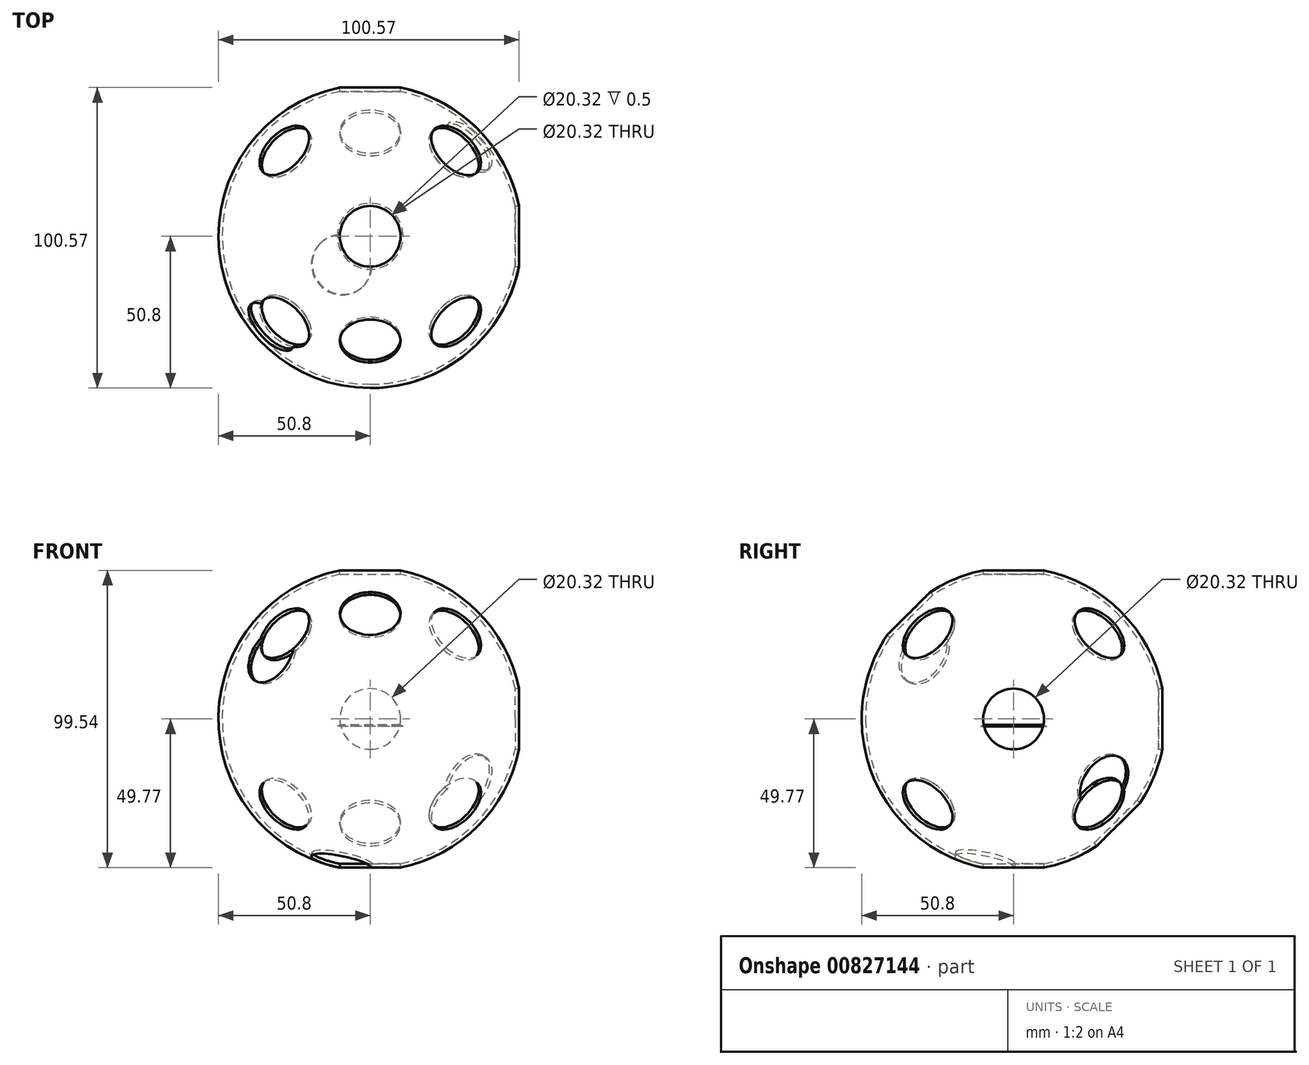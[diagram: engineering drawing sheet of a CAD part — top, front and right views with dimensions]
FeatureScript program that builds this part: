
annotation { "Feature Type Name" : "Feature", "Feature Type Description" : "" }
export const myFeature = defineFeature(function(context is Context, id is Id, definition is map)
    precondition{}
    {
        {
            assignVariable(context, id + "F0", {"name" : "SphereDiameter", "anyValue" : 4});
        }
        {
            assignVariable(context, id + "F1", {"name" : "BaseHeight", "anyValue" : getVariable(context, 'SphereDiameter') / 8});
        }
        {
            var Q0;
            Q0=qCreatedBy(makeId("Top.planeOp"),FACE);
            var sketch = newSketch(context, id + "F2", { "sketchPlane" : qUnion([Q0])});
            skArc(sketch, "E0", {"start": v(0, 50.8) * mm, "mid": v(-50.8, 0) * mm, "end": v(0, -50.8) * mm});
            skLineSegment(sketch, "E1", {"start": v(0, 50.8) * mm, "end": v(0, -50.8) * mm});
            skSolve(sketch);
        }
        {
            var Q0;
            Q0=qSketchRegion(id+"F2",true);
            var Q1;
            Q1=sQuery(id+"F2.wireOp",EDGE,"E1");
            revolve(context, id + "F3", {"surfaceOperationType" : NewSurfaceOperationType.NEW, "entities" : qUnion([Q0]), "axis" : qUnion([Q1]), "revolveType" : RevolveType.FULL});
        }
        {
            var Q0;
            Q0=qCreatedBy(makeId("Top.planeOp"),FACE);
            var sketch = newSketch(context, id + "F4", { "sketchPlane" : qUnion([Q0])});
            skLineSegment(sketch, "E2", {"start": v(0, 0) * mm, "end": v(0, 50.8) * mm});
            skLineSegment(sketch, "E3", {"start": v(0, 0) * mm, "end": v(0, -50.8) * mm});
            skLineSegment(sketch, "E4", {"start": v(0, 0) * mm, "end": v(50.8, 0) * mm});
            skLineSegment(sketch, "E5", {"start": v(0, 0) * mm, "end": v(-50.8, 0) * mm});
            skSolve(sketch);
        }
        {
            var Q0;
            Q0=qCreatedBy(makeId("Front.planeOp"),FACE);
            var sketch = newSketch(context, id + "F5", { "sketchPlane" : qUnion([Q0])});
            skLineSegment(sketch, "E6", {"start": v(0, 0) * mm, "end": v(0, 50.8) * mm});
            skLineSegment(sketch, "E7", {"start": v(0, 0) * mm, "end": v(0, -50.8) * mm});
            skSolve(sketch);
        }
        {
            var Q0;
            Q0=sQuery(id+"F5.wireOp",VERTEX,"E6.end");
            var Q1;
            Q1=sQuery(id+"F4.wireOp",VERTEX,"E3.end");
            var Q2;
            Q2=sQuery(id+"F4.wireOp",VERTEX,"E4.end");
            cPlane(context, id + "F6", {"entities" : qUnion([Q0, Q1, Q2]), "cplaneType" : CPlaneType.THREE_POINT, "offset" : 25.4 * mm, "width" : 152.4 * mm, "height" : 152.4 * mm});
        }
        {
            var Q0;
            Q0=qCreatedBy(id+"F6.planeOp",FACE);
            var sketch = newSketch(context, id + "F7", { "sketchPlane" : qUnion([Q0])});
            skLineSegment(sketch, "E8", {"start": v(-41.48, 0) * mm, "end": v(20.74, -35.92) * mm});
            skLineSegment(sketch, "E9", {"start": v(20.74, -35.92) * mm, "end": v(20.74, 35.92) * mm});
            skLineSegment(sketch, "E10", {"start": v(20.74, 35.92) * mm, "end": v(-41.48, 0) * mm});
            skLineSegment(sketch, "E11", {"start": v(20.74, 35.92) * mm, "end": v(0, 0) * mm});
            skSolve(sketch);
        }
        {
            var Q0;
            Q0=sQuery(id+"F5.wireOp",VERTEX,"E6.end");
            var Q1;
            Q1=sQuery(id+"F7.wireOp",VERTEX,"E11.end");
            var Q2;
            Q2=sQuery(id+"F4.wireOp",VERTEX,"E3.start");
            cPlane(context, id + "F8", {"entities" : qUnion([Q0, Q1, Q2]), "cplaneType" : CPlaneType.THREE_POINT, "offset" : 25.4 * mm, "width" : 152.4 * mm, "height" : 152.4 * mm});
        }
        {
            var Q0;
            Q0=qCreatedBy(id+"F8.planeOp",FACE);
            var sketch = newSketch(context, id + "F9", { "sketchPlane" : qUnion([Q0])});
            skLineSegment(sketch, "E12", {"start": v(0, 0) * mm, "end": v(23.95, 16.93) * mm});
            skLineSegment(sketch, "E13", {"start": v(10.37, 7.33) * mm, "end": v(23.95, 16.93) * mm});
            skLineSegment(sketch, "E14", {"start": v(0, 0) * mm, "end": v(-10.37, -7.33) * mm});
            skSolve(sketch);
        }
        {
            var Q0;
            Q0=sQuery(id+"F4.wireOp",VERTEX,"E2.end");
            var Q1;
            Q1=sQuery(id+"F5.wireOp",VERTEX,"E6.end");
            var Q2;
            Q2=sQuery(id+"F4.wireOp",VERTEX,"E5.end");
            cPlane(context, id + "F10", {"entities" : qUnion([Q0, Q1, Q2]), "cplaneType" : CPlaneType.THREE_POINT, "offset" : 25.4 * mm, "width" : 152.4 * mm, "height" : 152.4 * mm});
        }
        {
            var Q0;
            Q0=qCreatedBy(id+"F10.planeOp",FACE);
            var sketch = newSketch(context, id + "F11", { "sketchPlane" : qUnion([Q0])});
            skLineSegment(sketch, "E15", {"start": v(41.48, 0) * mm, "end": v(-20.74, 35.92) * mm});
            skLineSegment(sketch, "E16", {"start": v(-20.74, 35.92) * mm, "end": v(-20.74, -35.92) * mm});
            skLineSegment(sketch, "E17", {"start": v(-20.74, -35.92) * mm, "end": v(41.48, 0) * mm});
            skLineSegment(sketch, "E18", {"start": v(-20.74, 35.92) * mm, "end": v(0, 0) * mm});
            skSolve(sketch);
        }
        {
            var Q0;
            Q0=sQuery(id+"F5.wireOp",VERTEX,"E6.end");
            var Q1;
            Q1=qCreatedBy(makeId("Origin.pointOp"),VERTEX);
            var Q2;
            Q2=sQuery(id+"F11.wireOp",VERTEX,"E18.end");
            cPlane(context, id + "F12", {"entities" : qUnion([Q0, Q1, Q2]), "cplaneType" : CPlaneType.THREE_POINT, "offset" : 25.4 * mm, "width" : 152.4 * mm, "height" : 152.4 * mm});
        }
        {
            var Q0;
            Q0=qCreatedBy(id+"F12.planeOp",FACE);
            var sketch = newSketch(context, id + "F13", { "sketchPlane" : qUnion([Q0])});
            skLineSegment(sketch, "E19", {"start": v(0, 0) * mm, "end": v(-23.95, 16.93) * mm});
            skLineSegment(sketch, "E20", {"start": v(-23.95, 16.93) * mm, "end": v(-10.37, 7.33) * mm});
            skLineSegment(sketch, "E21", {"start": v(10.37, -7.33) * mm, "end": v(0, 0) * mm});
            skSolve(sketch);
        }
        {
            var Q0;
            Q0=sQuery(id+"F4.wireOp",VERTEX,"E2.end");
            var Q1;
            Q1=sQuery(id+"F5.wireOp",VERTEX,"E7.end");
            var Q2;
            Q2=sQuery(id+"F4.wireOp",VERTEX,"E4.end");
            cPlane(context, id + "F14", {"entities" : qUnion([Q0, Q1, Q2]), "cplaneType" : CPlaneType.THREE_POINT, "offset" : 25.4 * mm, "width" : 152.4 * mm, "height" : 152.4 * mm});
        }
        {
            var Q0;
            Q0=qCreatedBy(id+"F14.planeOp",FACE);
            var sketch = newSketch(context, id + "F15", { "sketchPlane" : qUnion([Q0])});
            skLineSegment(sketch, "E22", {"start": v(20.74, -35.92) * mm, "end": v(20.74, 35.92) * mm});
            skLineSegment(sketch, "E23", {"start": v(20.74, 35.92) * mm, "end": v(-41.48, 0) * mm});
            skLineSegment(sketch, "E24", {"start": v(-41.48, 0) * mm, "end": v(20.74, -35.92) * mm});
            skLineSegment(sketch, "E25", {"start": v(20.74, 35.92) * mm, "end": v(0, 0) * mm});
            skSolve(sketch);
        }
        {
            var Q0;
            Q0=sQuery(id+"F4.wireOp",VERTEX,"E3.start");
            var Q1;
            Q1=sQuery(id+"F4.wireOp",VERTEX,"E2.end");
            var Q2;
            Q2=sQuery(id+"F15.wireOp",VERTEX,"E25.end");
            cPlane(context, id + "F16", {"entities" : qUnion([Q0, Q1, Q2]), "cplaneType" : CPlaneType.THREE_POINT, "offset" : 25.4 * mm, "width" : 152.4 * mm, "height" : 152.4 * mm});
        }
        {
            var Q0;
            Q0=qCreatedBy(id+"F16.planeOp",FACE);
            var sketch = newSketch(context, id + "F17", { "sketchPlane" : qUnion([Q0])});
            skLineSegment(sketch, "E26", {"start": v(0, 0) * mm, "end": v(16.93, -23.95) * mm});
            skLineSegment(sketch, "E27", {"start": v(7.33, -10.37) * mm, "end": v(16.93, -23.95) * mm});
            skLineSegment(sketch, "E28", {"start": v(0, 0) * mm, "end": v(-7.33, 10.37) * mm});
            skSolve(sketch);
        }
        {
            var Q0;
            Q0=sQuery(id+"F5.wireOp",VERTEX,"E6.end");
            var Q1;
            Q1=sQuery(id+"F4.wireOp",VERTEX,"E4.end");
            var Q2;
            Q2=sQuery(id+"F4.wireOp",VERTEX,"E2.end");
            cPlane(context, id + "F18", {"entities" : qUnion([Q0, Q1, Q2]), "cplaneType" : CPlaneType.THREE_POINT, "offset" : 25.4 * mm, "width" : 152.4 * mm, "height" : 152.4 * mm});
        }
        {
            var Q0;
            Q0=qCreatedBy(id+"F18.planeOp",FACE);
            var sketch = newSketch(context, id + "F19", { "sketchPlane" : qUnion([Q0])});
            skLineSegment(sketch, "E29", {"start": v(-20.74, 35.92) * mm, "end": v(41.48, 0) * mm});
            skLineSegment(sketch, "E30", {"start": v(41.48, 0) * mm, "end": v(-20.74, -35.92) * mm});
            skLineSegment(sketch, "E31", {"start": v(-20.74, -35.92) * mm, "end": v(-20.74, 35.92) * mm});
            skLineSegment(sketch, "E32", {"start": v(-20.74, 35.92) * mm, "end": v(0, 0) * mm});
            skSolve(sketch);
        }
        {
            var Q0;
            Q0=sQuery(id+"F5.wireOp",VERTEX,"E6.end");
            var Q1;
            Q1=sQuery(id+"F19.wireOp",VERTEX,"E32.end");
            var Q2;
            Q2=sQuery(id+"F4.wireOp",VERTEX,"E3.start");
            cPlane(context, id + "F20", {"entities" : qUnion([Q0, Q1, Q2]), "cplaneType" : CPlaneType.THREE_POINT, "offset" : 25.4 * mm, "width" : 152.4 * mm, "height" : 152.4 * mm});
        }
        {
            var Q0;
            Q0=qCreatedBy(id+"F20.planeOp",FACE);
            var sketch = newSketch(context, id + "F21", { "sketchPlane" : qUnion([Q0])});
            skLineSegment(sketch, "E33", {"start": v(0, 0) * mm, "end": v(23.95, 16.93) * mm});
            skLineSegment(sketch, "E34", {"start": v(10.37, 7.33) * mm, "end": v(23.95, 16.93) * mm});
            skLineSegment(sketch, "E35", {"start": v(0, 0) * mm, "end": v(-10.37, -7.33) * mm});
            skSolve(sketch);
        }
        {
            var Q0;
            Q0=qCreatedBy(makeId("Top.planeOp"),FACE);
            var Q1;
            Q1=sQuery(id+"F5.wireOp",VERTEX,"E6.end");
            cPlane(context, id + "F22", {"entities" : qUnion([Q0, Q1]), "cplaneType" : CPlaneType.PLANE_POINT, "offset" : 25.4 * mm, "width" : 152.4 * mm, "height" : 152.4 * mm});
        }
        {
            var Q0;
            Q0=qCreatedBy(id+"F22.planeOp",FACE);
            var sketch = newSketch(context, id + "F23", { "sketchPlane" : qUnion([Q0])});
            skCircle(sketch, "E36", {"center": v(0, 0) * mm, "radius": 10.16 * mm});
            skSolve(sketch);
        }
        {
            var Q0;
            Q0=qSketchRegion(id+"F23",true);
            extrude(context, id + "F24", {"entities" : qUnion([Q0]), "operationType" : NewBodyOperationType.REMOVE, "endBound" : BoundingType.SYMMETRIC, "oppositeDirection" : true, "depth" : 76.2 * mm, "offsetDistance" : 25.4 * mm});
        }
        {
            var Q0;
            Q0=qCreatedBy(makeId("Right.planeOp"),FACE);
            var Q1;
            Q1=sQuery(id+"F4.wireOp",VERTEX,"E4.end");
            cPlane(context, id + "F25", {"entities" : qUnion([Q0, Q1]), "cplaneType" : CPlaneType.PLANE_POINT, "offset" : 25.4 * mm, "width" : 152.4 * mm, "height" : 152.4 * mm});
        }
        {
            var Q0;
            Q0=qCreatedBy(id+"F25.planeOp",FACE);
            var sketch = newSketch(context, id + "F26", { "sketchPlane" : qUnion([Q0])});
            skCircle(sketch, "E37", {"center": v(0, 0) * mm, "radius": 10.16 * mm});
            skSolve(sketch);
        }
        {
            var Q0;
            Q0=qSketchRegion(id+"F26",true);
            extrude(context, id + "F27", {"entities" : qUnion([Q0]), "operationType" : NewBodyOperationType.REMOVE, "endBound" : BoundingType.SYMMETRIC, "oppositeDirection" : true, "depth" : 76.2 * mm, "offsetDistance" : 25.4 * mm});
        }
        {
            var Q0;
            Q0=qCreatedBy(makeId("Front.planeOp"),FACE);
            var Q1;
            Q1=sQuery(id+"F4.wireOp",VERTEX,"E2.end");
            cPlane(context, id + "F28", {"entities" : qUnion([Q0, Q1]), "cplaneType" : CPlaneType.PLANE_POINT, "offset" : 25.4 * mm, "width" : 152.4 * mm, "height" : 152.4 * mm});
        }
        {
            var Q0;
            Q0=qCreatedBy(id+"F28.planeOp",FACE);
            var sketch = newSketch(context, id + "F29", { "sketchPlane" : qUnion([Q0])});
            skCircle(sketch, "E38", {"center": v(0, 0) * mm, "radius": 10.16 * mm});
            skSolve(sketch);
        }
        {
            var Q0;
            Q0=qSketchRegion(id+"F29",true);
            extrude(context, id + "F30", {"entities" : qUnion([Q0]), "operationType" : NewBodyOperationType.REMOVE, "endBound" : BoundingType.SYMMETRIC, "depth" : 76.2 * mm, "offsetDistance" : 25.4 * mm});
        }
        {
            var Q0;
            Q0=qCreatedBy(id+"F6.planeOp",FACE);
            var Q1;
            Q1=sQuery(id+"F9.wireOp",VERTEX,"E13.end");
            cPlane(context, id + "F31", {"entities" : qUnion([Q0, Q1]), "cplaneType" : CPlaneType.PLANE_POINT, "offset" : 25.4 * mm, "width" : 152.4 * mm, "height" : 152.4 * mm});
        }
        {
            var Q0;
            Q0=qCreatedBy(id+"F31.planeOp",FACE);
            var sketch = newSketch(context, id + "F32", { "sketchPlane" : qUnion([Q0])});
            skCircle(sketch, "E39", {"center": v(0, 0) * mm, "radius": 10.16 * mm});
            skSolve(sketch);
        }
        {
            var Q0;
            Q0=qSketchRegion(id+"F32",true);
            extrude(context, id + "F33", {"entities" : qUnion([Q0]), "operationType" : NewBodyOperationType.REMOVE, "endBound" : BoundingType.SYMMETRIC, "depth" : 254 * mm, "offsetDistance" : 25.4 * mm});
        }
        {
            var Q0;
            Q0=qCreatedBy(id+"F10.planeOp",FACE);
            var Q1;
            Q1=sQuery(id+"F13.wireOp",VERTEX,"E20.start");
            cPlane(context, id + "F34", {"entities" : qUnion([Q0, Q1]), "cplaneType" : CPlaneType.PLANE_POINT, "offset" : 25.4 * mm, "width" : 152.4 * mm, "height" : 152.4 * mm});
        }
        {
            var Q0;
            Q0=qCreatedBy(id+"F34.planeOp",FACE);
            var sketch = newSketch(context, id + "F35", { "sketchPlane" : qUnion([Q0])});
            skCircle(sketch, "E40", {"center": v(0, 0) * mm, "radius": 10.16 * mm});
            skSolve(sketch);
        }
        {
            var Q0;
            Q0=qSketchRegion(id+"F35",true);
            extrude(context, id + "F36", {"entities" : qUnion([Q0]), "operationType" : NewBodyOperationType.REMOVE, "endBound" : BoundingType.SYMMETRIC, "depth" : 254 * mm, "offsetDistance" : 25.4 * mm});
        }
        {
            var Q0;
            Q0=qCreatedBy(id+"F18.planeOp",FACE);
            var Q1;
            Q1=sQuery(id+"F21.wireOp",VERTEX,"E34.end");
            cPlane(context, id + "F37", {"entities" : qUnion([Q0, Q1]), "cplaneType" : CPlaneType.PLANE_POINT, "offset" : 25.4 * mm, "width" : 152.4 * mm, "height" : 152.4 * mm});
        }
        {
            var Q0;
            Q0=qCreatedBy(id+"F37.planeOp",FACE);
            var sketch = newSketch(context, id + "F38", { "sketchPlane" : qUnion([Q0])});
            skCircle(sketch, "E41", {"center": v(0, 0) * mm, "radius": 10.16 * mm});
            skSolve(sketch);
        }
        {
            var Q0;
            Q0=qSketchRegion(id+"F38",true);
            extrude(context, id + "F39", {"entities" : qUnion([Q0]), "operationType" : NewBodyOperationType.REMOVE, "endBound" : BoundingType.SYMMETRIC, "depth" : 254 * mm, "offsetDistance" : 25.4 * mm});
        }
        {
            var Q0;
            Q0=qCreatedBy(id+"F14.planeOp",FACE);
            var Q1;
            Q1=sQuery(id+"F17.wireOp",VERTEX,"E27.end");
            cPlane(context, id + "F40", {"entities" : qUnion([Q0, Q1]), "cplaneType" : CPlaneType.PLANE_POINT, "offset" : 25.4 * mm, "width" : 152.4 * mm, "height" : 152.4 * mm});
        }
        {
            var Q0;
            Q0=qCreatedBy(id+"F40.planeOp",FACE);
            var sketch = newSketch(context, id + "F41", { "sketchPlane" : qUnion([Q0])});
            skCircle(sketch, "E42", {"center": v(0, 0) * mm, "radius": 10.16 * mm});
            skSolve(sketch);
        }
        {
            var Q0;
            Q0=qSketchRegion(id+"F41",true);
            extrude(context, id + "F42", {"entities" : qUnion([Q0]), "operationType" : NewBodyOperationType.REMOVE, "endBound" : BoundingType.SYMMETRIC, "depth" : 254 * mm, "offsetDistance" : 25.4 * mm});
        }
        {
            var Q0;
            Q0=qCreatedBy(makeId("Top.planeOp"),FACE);
            var sketch = newSketch(context, id + "F43", { "sketchPlane" : qUnion([Q0])});
            skArc(sketch, "E43", {"start": v(0, 49.53) * mm, "mid": v(-49.53, 0) * mm, "end": v(0, -49.53) * mm});
            skLineSegment(sketch, "E44", {"start": v(0, 49.53) * mm, "end": v(0, -49.53) * mm});
            skSolve(sketch);
        }
        {
            var Q0;
            Q0=qSketchRegion(id+"F43",true);
            var Q1;
            Q1=sQuery(id+"F4.wireOp",EDGE,"E2");
            revolve(context, id + "F44", {"operationType" : NewBodyOperationType.REMOVE, "surfaceOperationType" : NewSurfaceOperationType.NEW, "entities" : qUnion([Q0]), "axis" : qUnion([Q1]), "revolveType" : RevolveType.FULL, "oppositeDirection" : true});
        }
        {
            var Q0;
            Q0=sQuery(id+"F13.wireOp",VERTEX,"E20.start");
            var Q1;
            Q1=sQuery(id+"F29.wireOp",VERTEX,"E38.center");
            var Q2;
            Q2=sQuery(id+"F21.wireOp",VERTEX,"E34.end");
            cPlane(context, id + "F45", {"entities" : qUnion([Q0, Q1, Q2]), "cplaneType" : CPlaneType.THREE_POINT, "offset" : 25.4 * mm, "width" : 152.4 * mm, "height" : 152.4 * mm});
        }
        {
            var Q0;
            Q0=qCreatedBy(id+"F45.planeOp",FACE);
            var sketch = newSketch(context, id + "F46", { "sketchPlane" : qUnion([Q0])});
            skLineSegment(sketch, "E45", {"start": v(7.33, 6.01) * mm, "end": v(-7.33, 6.01) * mm});
            skLineSegment(sketch, "E46", {"start": v(0, 50.1) * mm, "end": v(0, 6.01) * mm});
            skSolve(sketch);
        }
        {
            var Q0;
            Q0=sQuery(id+"F5.wireOp",VERTEX,"E6.end");
            var Q1;
            Q1=sQuery(id+"F21.wireOp",VERTEX,"E34.end");
            var Q2;
            Q2=sQuery(id+"F13.wireOp",VERTEX,"E20.start");
            cPlane(context, id + "F47", {"entities" : qUnion([Q0, Q1, Q2]), "cplaneType" : CPlaneType.THREE_POINT, "offset" : 25.4 * mm, "width" : 152.4 * mm, "height" : 152.4 * mm});
        }
        {
            var Q0;
            Q0=qCreatedBy(id+"F47.planeOp",FACE);
            var sketch = newSketch(context, id + "F48", { "sketchPlane" : qUnion([Q0])});
            skLineSegment(sketch, "E47", {"start": v(0, 50.1) * mm, "end": v(0, 6.01) * mm});
            skSolve(sketch);
        }
        {
            var Q0;
            Q0=qCreatedBy(id+"F47.planeOp",FACE);
            var sketch = newSketch(context, id + "F49", { "sketchPlane" : qUnion([Q0])});
            skLineSegment(sketch, "E48", {"start": v(0, -1.43) * mm, "end": v(0, 6.01) * mm});
            skSolve(sketch);
        }
        {
            var Q0;
            Q0=qCreatedBy(id+"F45.planeOp",FACE);
            var sketch = newSketch(context, id + "F50", { "sketchPlane" : qUnion([Q0])});
            skLineSegment(sketch, "E49", {"start": v(0, 6.01) * mm, "end": v(0, -1.43) * mm});
            skSolve(sketch);
        }
        {
            var Q0;
            Q0=sQuery(id+"F13.wireOp",VERTEX,"E19.start");
            var Q1;
            Q1=sQuery(id+"F13.wireOp",VERTEX,"E20.start");
            var Q2;
            Q2=sQuery(id+"F21.wireOp",VERTEX,"E34.end");
            cPlane(context, id + "F51", {"entities" : qUnion([Q0, Q1, Q2]), "cplaneType" : CPlaneType.THREE_POINT, "offset" : 25.4 * mm, "width" : 152.4 * mm, "height" : 152.4 * mm});
        }
        {
            var Q0;
            Q0=sQuery(id+"F50.wireOp",VERTEX,"E49.start");
            var Q1;
            Q1=sQuery(id+"F49.wireOp",VERTEX,"E48.start");
            var Q2;
            Q2=sQuery(id+"F49.wireOp",VERTEX,"E48.end");
            cPlane(context, id + "F52", {"entities" : qUnion([Q0, Q1, Q2]), "cplaneType" : CPlaneType.THREE_POINT, "offset" : 25.4 * mm, "width" : 152.4 * mm, "height" : 152.4 * mm});
        }
        {
            var Q0;
            Q0=qCreatedBy(id+"F52.planeOp",FACE);
            var sketch = newSketch(context, id + "F53", { "sketchPlane" : qUnion([Q0])});
            skLineSegment(sketch, "E50", {"start": v(1.61, 15.15) * mm, "end": v(15.53, 1.33) * mm});
            skSolve(sketch);
        }
        {
            var Q0;
            Q0=sQuery(id+"F53.wireOp",EDGE,"E50");
            var Q1;
            Q1=qCreatedBy(id+"F45.planeOp",FACE);
            cPlane(context, id + "F54", {"entities" : qUnion([Q0, Q1]), "cplaneType" : CPlaneType.LINE_ANGLE, "offset" : 25.4 * mm, "angle" : 0 * degree, "width" : 152.4 * mm, "height" : 152.4 * mm});
        }
        {
            var Q0;
            Q0=qCreatedBy(id+"F54.planeOp",FACE);
            var sketch = newSketch(context, id + "F55", { "sketchPlane" : qUnion([Q0])});
            skCircle(sketch, "E51", {"center": v(0, 0) * mm, "radius": 10.16 * mm});
            skSolve(sketch);
        }
        {
            var Q0;
            Q0=qSketchRegion(id+"F55",true);
            extrude(context, id + "F56", {"entities" : qUnion([Q0]), "operationType" : NewBodyOperationType.REMOVE, "endBound" : BoundingType.SYMMETRIC, "depth" : 127 * mm, "offsetDistance" : 25.4 * mm});
        }
        {
            var Q0;
            Q0=sQuery(id+"F9.wireOp",VERTEX,"E13.end");
            var Q1;
            Q1=qCreatedBy(makeId("Origin.pointOp"),VERTEX);
            var Q2;
            Q2=sQuery(id+"F21.wireOp",VERTEX,"E34.end");
            cPlane(context, id + "F57", {"entities" : qUnion([Q0, Q1, Q2]), "cplaneType" : CPlaneType.THREE_POINT, "offset" : 25.4 * mm, "width" : 152.4 * mm, "height" : 152.4 * mm});
        }
        {
            var Q0;
            Q0=qCreatedBy(id+"F57.planeOp",FACE);
            var sketch = newSketch(context, id + "F58", { "sketchPlane" : qUnion([Q0])});
            skLineSegment(sketch, "E52", {"start": v(10.37, 7.33) * mm, "end": v(10.37, -7.33) * mm});
            skLineSegment(sketch, "E53", {"start": v(0, 0) * mm, "end": v(10.37, 0) * mm});
            skSolve(sketch);
        }
        {
            var Q0;
            Q0=sQuery(id+"F58.wireOp",VERTEX,"E53.end");
            var Q1;
            Q1=sQuery(id+"F5.wireOp",VERTEX,"E6.end");
            var Q2;
            Q2=sQuery(id+"F9.wireOp",VERTEX,"E12.start");
            cPlane(context, id + "F59", {"entities" : qUnion([Q0, Q1, Q2]), "cplaneType" : CPlaneType.THREE_POINT, "offset" : 25.4 * mm, "width" : 152.4 * mm, "height" : 152.4 * mm});
        }
        {
            var Q0;
            Q0=qCreatedBy(id+"F59.planeOp",FACE);
            var sketch = newSketch(context, id + "F60", { "sketchPlane" : qUnion([Q0])});
            skLineSegment(sketch, "E54", {"start": v(-7.33, 7.33) * mm, "end": v(0, 50.8) * mm});
            skLineSegment(sketch, "E55", {"start": v(-7.33, 7.33) * mm, "end": v(-50.8, 0) * mm});
            skLineSegment(sketch, "E56", {"start": v(0, 14.66) * mm, "end": v(-14.66, 0) * mm});
            skSolve(sketch);
        }
        {
            var Q0;
            Q0=sQuery(id+"F58.wireOp",VERTEX,"E53.end");
            var Q1;
            Q1=sQuery(id+"F60.wireOp",VERTEX,"E56.start");
            var Q2;
            Q2=sQuery(id+"F9.wireOp",VERTEX,"E13.end");
            cPlane(context, id + "F61", {"entities" : qUnion([Q0, Q1, Q2]), "cplaneType" : CPlaneType.THREE_POINT, "offset" : 25.4 * mm, "width" : 152.4 * mm, "height" : 152.4 * mm});
        }
        {
            var Q0;
            Q0=qCreatedBy(id+"F61.planeOp",FACE);
            var sketch = newSketch(context, id + "F62", { "sketchPlane" : qUnion([Q0])});
            skCircle(sketch, "E57", {"center": v(0, 0) * mm, "radius": 10.16 * mm});
            skSolve(sketch);
        }
        {
            var Q0;
            Q0=qSketchRegion(id+"F62",true);
            extrude(context, id + "F63", {"entities" : qUnion([Q0]), "operationType" : NewBodyOperationType.REMOVE, "endBound" : BoundingType.SYMMETRIC, "depth" : 127 * mm, "offsetDistance" : 25.4 * mm});
        }
        {
            var Q0;
            Q0=sQuery(id+"F4.wireOp",VERTEX,"E5.end");
            var Q1;
            Q1=qCreatedBy(makeId("Origin.pointOp"),VERTEX);
            var Q2;
            Q2=sQuery(id+"F4.wireOp",VERTEX,"E3.end");
            cPlane(context, id + "F64", {"entities" : qUnion([Q0, Q1, Q2]), "cplaneType" : CPlaneType.THREE_POINT, "offset" : 25.4 * mm, "width" : 152.4 * mm, "height" : 152.4 * mm});
        }
        {
            var Q0;
            Q0=qCreatedBy(id+"F64.planeOp",FACE);
            var sketch = newSketch(context, id + "F65", { "sketchPlane" : qUnion([Q0])});
            skLineSegment(sketch, "E58", {"start": v(0, -50.8) * mm, "end": v(-50.8, 0) * mm});
            skLineSegment(sketch, "E59", {"start": v(0, 0) * mm, "end": v(-25.4, -25.4) * mm});
            skSolve(sketch);
        }
        {
            var Q0;
            Q0=sQuery(id+"F17.wireOp",VERTEX,"E28.end");
            var Q1;
            Q1=sQuery(id+"F21.wireOp",VERTEX,"E35.end");
            var Q2;
            Q2=sQuery(id+"F58.wireOp",VERTEX,"E53.start");
            cPlane(context, id + "F66", {"entities" : qUnion([Q0, Q1, Q2]), "cplaneType" : CPlaneType.THREE_POINT, "offset" : 25.4 * mm, "width" : 152.4 * mm, "height" : 152.4 * mm});
        }
        {
            var Q0;
            Q0=qCreatedBy(id+"F66.planeOp",FACE);
            var sketch = newSketch(context, id + "F67", { "sketchPlane" : qUnion([Q0])});
            skLineSegment(sketch, "E60", {"start": v(10.37, -7.33) * mm, "end": v(10.37, 7.33) * mm});
            skLineSegment(sketch, "E61", {"start": v(10.37, 0) * mm, "end": v(35.92, 0) * mm});
            skPoint(sketch, "E61.endSnap0", {"position": v(10.37, 0) * mm});
            skSolve(sketch);
        }
        {
            var Q0;
            Q0=qCreatedBy(id+"F64.planeOp",FACE);
            var sketch = newSketch(context, id + "F68", { "sketchPlane" : qUnion([Q0])});
            skLineSegment(sketch, "E62", {"start": v(-14.66, 0) * mm, "end": v(0, -14.66) * mm});
            skLineSegment(sketch, "E63", {"start": v(-14.66, 0) * mm, "end": v(-50.8, 0) * mm});
            skLineSegment(sketch, "E64", {"start": v(-14.66, 0) * mm, "end": v(-14.66, 0) * mm});
            skLineSegment(sketch, "E65", {"start": v(0, -14.66) * mm, "end": v(0, -50.8) * mm});
            skSolve(sketch);
        }
        {
            var Q0;
            Q0=sQuery(id+"F68.wireOp",VERTEX,"E63.end");
            var Q1;
            Q1=sQuery(id+"F68.wireOp",VERTEX,"E65.end");
            var Q2;
            Q2=sQuery(id+"F21.wireOp",VERTEX,"E35.end");
            cPlane(context, id + "F69", {"entities" : qUnion([Q0, Q1, Q2]), "cplaneType" : CPlaneType.THREE_POINT, "offset" : 25.4 * mm, "width" : 152.4 * mm, "height" : 152.4 * mm});
        }
        {
            var Q0;
            Q0=qCreatedBy(id+"F69.planeOp",FACE);
            var sketch = newSketch(context, id + "F70", { "sketchPlane" : qUnion([Q0])});
            skCircle(sketch, "E66", {"center": v(0, 0) * mm, "radius": 10.16 * mm});
            skSolve(sketch);
        }
        {
            var Q0;
            Q0=qSketchRegion(id+"F70",true);
            extrude(context, id + "F71", {"entities" : qUnion([Q0]), "operationType" : NewBodyOperationType.REMOVE, "endBound" : BoundingType.SYMMETRIC, "oppositeDirection" : true, "depth" : 101.6 * mm, "offsetDistance" : 25.4 * mm});
        }
        {
            var Q0;
            Q0=qCreatedBy(makeId("Top.planeOp"),FACE);
            cPlane(context, id + "F72", {"entities" : qUnion([Q0]), "cplaneType" : CPlaneType.OFFSET, "offset" : ((getVariable(context, 'SphereDiameter') / 2) - (getVariable(context, 'SphereDiameter') / 90)) * mm, "oppositeDirection" : true, "width" : 152.4 * mm, "height" : 152.4 * mm});
        }
        {
            var Q0;
            Q0=qCreatedBy(id+"F72.planeOp",FACE);
            var sketch = newSketch(context, id + "F73", { "sketchPlane" : qUnion([Q0])});
            skCircle(sketch, "E67", {"center": v(0, 0) * mm, "radius": 10.16 * mm});
            skCircle(sketch, "E68", {"center": v(0, 0) * mm, "radius": 2.86 * mm});
            skSolve(sketch);
        }
        {
            var Q0;
            Q0=qSketchRegion(id+"F73",true);
            extrude(context, id + "F74", {"entities" : qUnion([Q0]), "operationType" : NewBodyOperationType.ADD, "oppositeDirection" : true, "depth" : (getVariable(context, 'BaseHeight')) * mm, "offsetDistance" : 25.4 * mm, "hasDraft" : true, "draftAngle" : 60 * degree});
        }
        {
            var Q0;
            Q0=qCreatedBy(makeId("Top.planeOp"),FACE);
            var sketch = newSketch(context, id + "F75", { "sketchPlane" : qUnion([Q0])});
            skCircle(sketch, "E69", {"center": v(0, 0) * mm, "radius": 10.16 * mm});
            skSolve(sketch);
        }
        {
            var Q0;
            Q0=qSketchRegion(id+"F75",true);
            extrude(context, id + "F76", {"entities" : qUnion([Q0]), "operationType" : NewBodyOperationType.REMOVE, "endBound" : BoundingType.THROUGH_ALL, "oppositeDirection" : true, "depth" : (getVariable(context, 'SphereDiameter') * 3) * mm, "offsetDistance" : 25.4 * mm});
        }
    });
